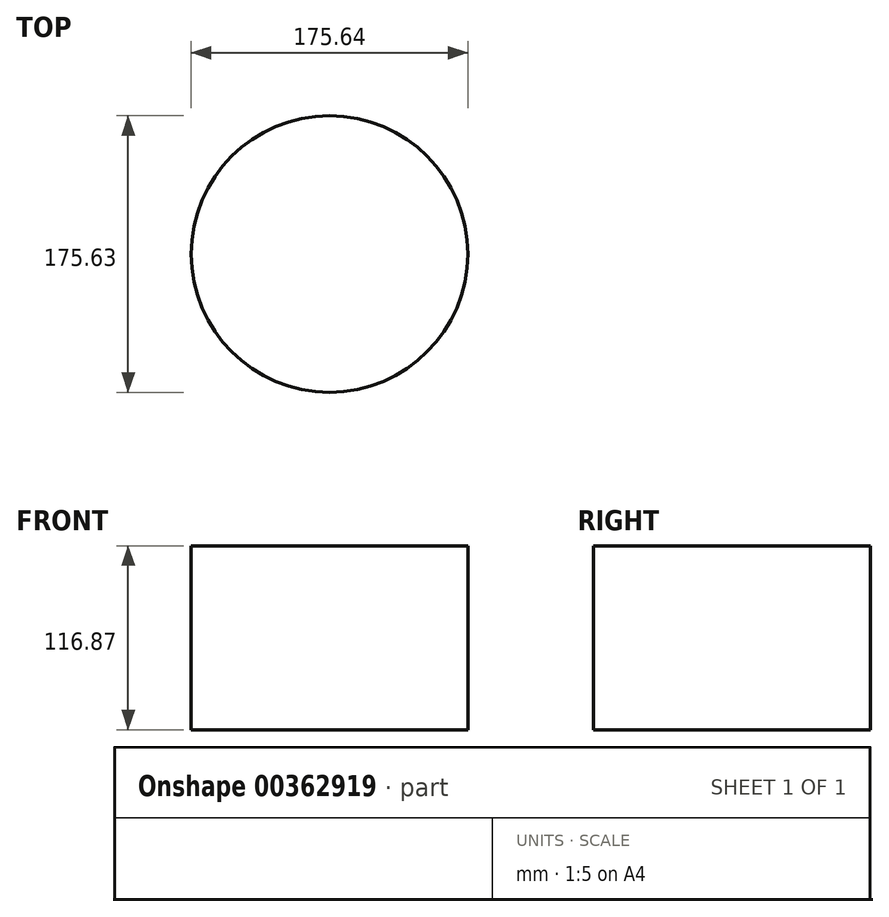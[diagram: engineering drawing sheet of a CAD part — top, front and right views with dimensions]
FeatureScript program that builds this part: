
annotation { "Feature Type Name" : "Feature", "Feature Type Description" : "" }
export const myFeature = defineFeature(function(context is Context, id is Id, definition is map)
    precondition{}
    {
        {
            var Q0;
            Q0=qCreatedBy(makeId("Top.planeOp"),FACE);
            var sketch = newSketch(context, id + "F0", { "sketchPlane" : qUnion([Q0])});
            skCircle(sketch, "E0", {"center": v(-12.7, -13.22) * mm, "radius": 87.82 * mm});
            skSolve(sketch);
        }
        {
            var Q0;
            Q0 = qSketchRegion(id + "F0", true);
            extrude(context, id + "F1", {"entities" : qUnion([Q0]), "depth" : 116.87 * mm});
        }
    });
